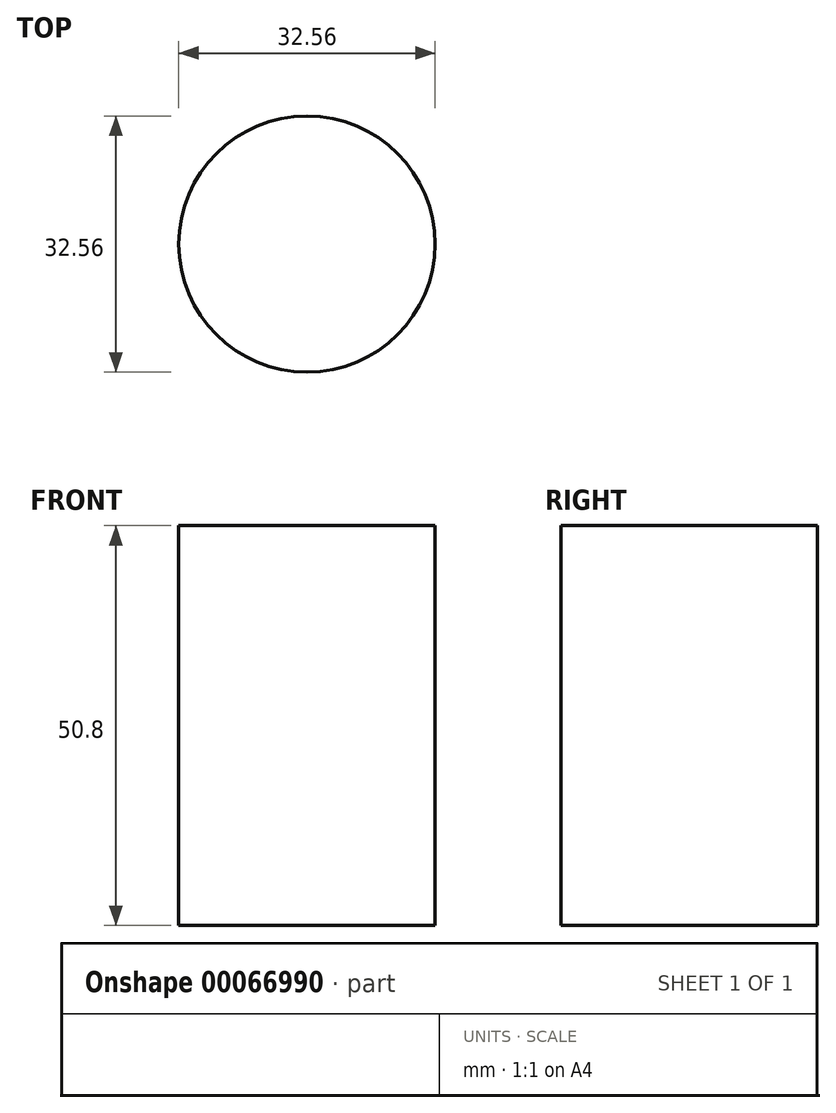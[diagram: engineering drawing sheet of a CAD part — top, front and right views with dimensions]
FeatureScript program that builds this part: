
annotation { "Feature Type Name" : "Feature", "Feature Type Description" : "" }
export const myFeature = defineFeature(function(context is Context, id is Id, definition is map)
    precondition{}
    {
        {
            var Q0;
            Q0=qCreatedBy(makeId("Top.planeOp"),FACE);
            var sketch = newSketch(context, id + "F0", { "sketchPlane" : qUnion([Q0])});
            skCircle(sketch, "E0", {"center": v(0, 0) * mm, "radius": 16.28 * mm});
            skSolve(sketch);
        }
        {
            var Q0;
            Q0=makeQuery(id+"F0.imprint","IMPRINT",FACE,{"disambiguationData":[TD([[makeQuery(id+"F0.imprint","IMPRINT",EDGE,{"derivedFrom":sQuery(id+"F0.wireOp",EDGE,"E0")}),1.0]])]});
            extrude(context, id + "F1", {"entities" : qUnion([Q0]), "depth" : 50.8 * mm});
        }
    });
